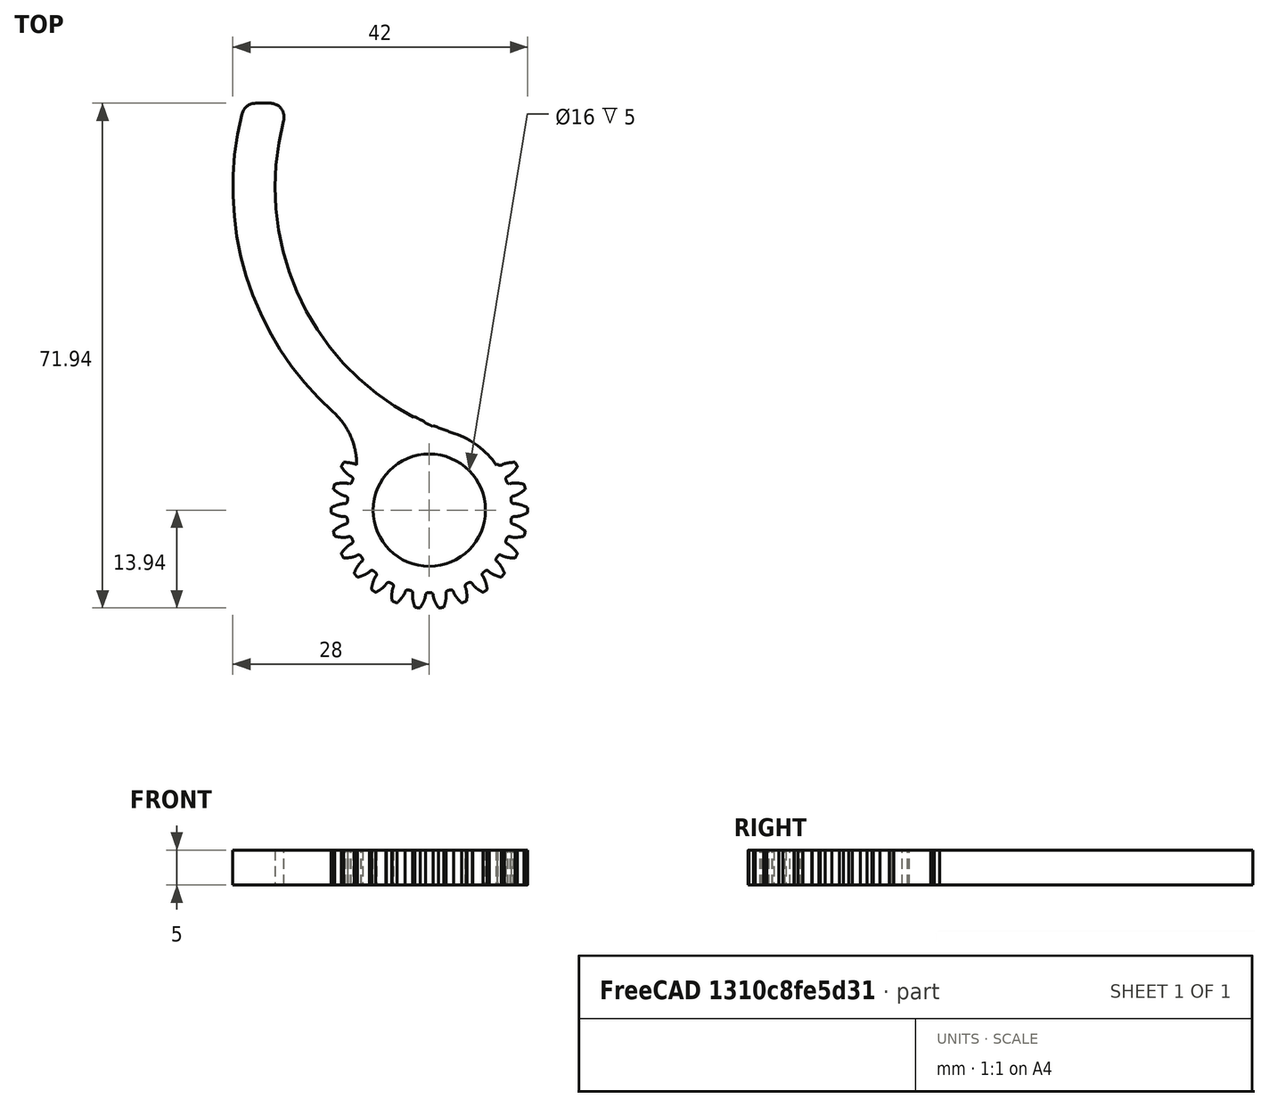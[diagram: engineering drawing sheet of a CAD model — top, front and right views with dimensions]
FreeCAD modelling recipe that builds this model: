
FCSTD DOCUMENT  (FreeCAD 1.0R39109 (Git))
Label: BrasV1_R
License: All rights reserved
LicenseURL: https://en.wikipedia.org/wiki/All_rights_reserved
objects: Sketcher::SketchObject×3, PartDesign::Pad×2, PartDesign::Fillet×2, PartDesign::Pocket×2, PartDesign::Chamfer×1, PartDesign::Line×1, Part::Part2DObjectPython×1, Mesh::Feature×1, PartDesign::CoordinateSystem×1, PartDesign::Body×1
note: 31 computed .brp shape members not serialized (recipe doc carries the construction recipe); baked Part::Feature solids carry a one-line shape summary decoded from their .brp

FEATURE [Sketcher::SketchObject] Sketch
  ArcFitTolerance = 0
  AttachmentSupport = -> [XY_Plane]
  FullyConstrained = true
  MakeInternals = false
  MapMode = 5
  sketch-geometry (5):
    g0: ArcOfCircle CenterX=0 CenterY=0 CenterZ=0 NormalX=0 NormalY=0 NormalZ=1 AngleXU=0 Radius=37 StartAngle=2.8113 EndAngle=4.39717
    g1: Circle CenterX=-15 CenterY=-46 CenterZ=0 NormalX=0 NormalY=0 NormalZ=1 AngleXU=0 Radius=8
    g2: ArcOfCircle CenterX=-15 CenterY=-46 CenterZ=0 NormalX=0 NormalY=0 NormalZ=1 AngleXU=0 Radius=11.3839 StartAngle=2.22683 EndAngle=7.53877
    g3: ArcOfCircle CenterX=0 CenterY=0 CenterZ=0 NormalX=0 NormalY=0 NormalZ=1 AngleXU=0 Radius=43 StartAngle=2.85877 EndAngle=4.17683
    g4: LineSegment StartX=-41.2916 StartY=12 StartZ=0 EndX=-35 EndY=12 EndZ=0
  constraints (14):
    c: Coincident(g0,g-1)
    c: Radius(g0) = 37
    c: Distance(g0,g-2) = 35
    c: Diameter(g1) = 16
    c: Distance(g1,g-2) = 15
    c: Coincident(g2,g1)
    c: Tangent(g2,g0) = 1.5708
    c: Coincident(g3,g0)
    c: Coincident(g2,g3)
    c: Radius(g3) = 43
    c: Coincident(g4,g3)
    c: Coincident(g4,g0)
    c: Horizontal(g4)
    c: Distance(g1,g-1) = 46
FEATURE [PartDesign::Pad] Pad
  Direction = (0,0,1)
  Length = 5
  Length2 = 10
  Midplane = true
  Profile = -> Sketch
  ReferenceAxis = -> Sketch [N_Axis]
  Suppressed = false
  Type = 0
FEATURE [PartDesign::Fillet] Fillet
  Base = -> Pad [Edge8]
  BaseFeature = -> Pad
  Radius = 10
  SupportTransform = false
  Suppressed = false
  UseAllEdges = false
FEATURE [PartDesign::Fillet] Fillet001
  Base = -> Fillet [Edge17,Edge12]
  BaseFeature = -> Fillet
  Radius = 2
  SupportTransform = false
  Suppressed = false
  UseAllEdges = false
FEATURE [PartDesign::Chamfer] Chamfer
  Angle = 45
  Base = -> Fillet001 [Edge24,Edge8]
  BaseFeature = -> Fillet001
  ChamferType = 0
  FlipDirection = false
  Size = 0.8
  Size2 = 1
  SupportTransform = false
  Suppressed = false
  UseAllEdges = false
FEATURE [PartDesign::Line] DatumLine
  AttacherType = Attacher::AttachEngineLine
  AttachmentSupport = -> [Chamfer]
  Length = 20
  MapMode = 42
  Placement = pos=(-15,-46,-1e-16) rot=(0,0,1;0rad)
  ResizeMode = 0
FEATURE [Part::Part2DObjectPython] InvoluteGear  # Draft 2D object (typed FeaturePython)
  AddendumCoefficient = 1
  DedendumCoefficient = 1.25
  ExternalGear = true
  HighPrecision = true
  Modules = 1
  NumberOfTeeth = 26
  Placement = pos=(-15,-46,0) rot=(0,0,20;0rad)
  PressureAngle = 20
  ProfileShiftCoefficient = 0
  RootFilletCoefficient = 0.38
FEATURE [PartDesign::Pad] Pad001
  BaseFeature = -> Chamfer
  Direction = (0,0,1)
  Length = 5
  Length2 = 10
  Midplane = true
  Profile = -> InvoluteGear
  ReferenceAxis = -> InvoluteGear [N_Axis]
  Suppressed = false
  Type = 0
FEATURE [Sketcher::SketchObject] Sketch001
  ArcFitTolerance = 0
  AttachmentSupport = -> [Pad001]
  FullyConstrained = false
  MakeInternals = false
  MapMode = 5
  Placement = pos=(0,0,2.5) rot=(0,0,1;0rad)
  sketch-geometry (1):
    g0: Circle CenterX=-15 CenterY=-46 CenterZ=0 NormalX=0 NormalY=0 NormalZ=1 AngleXU=0 Radius=8
  constraints (1):
    c: Diameter(g0) = 16
FEATURE [PartDesign::Pocket] Pocket
  BaseFeature = -> Pad001
  Direction = (0,0,-1)
  Length = 5
  Length2 = 5
  Profile = -> Sketch001
  ReferenceAxis = -> Sketch001 [N_Axis]
  Suppressed = false
  Type = 1
FEATURE [Sketcher::SketchObject] Sketch002
  ArcFitTolerance = 0
  AttachmentSupport = -> [Pocket]
  ExternalGeometry = -> [Pocket]
  FullyConstrained = true
  MakeInternals = false
  MapMode = 5
  Placement = pos=(0,0,2.5) rot=(0,0,1;0rad)
  sketch-geometry (4):
    g0: ArcOfCircle CenterX=-15 CenterY=-46 CenterZ=0 NormalX=0 NormalY=0 NormalZ=1 AngleXU=0 Radius=11.5 StartAngle=0.593412 EndAngle=1.25558
    g1: ArcOfCircle CenterX=-15 CenterY=-46 CenterZ=0 NormalX=0 NormalY=0 NormalZ=1 AngleXU=0 Radius=15 StartAngle=0.593412 EndAngle=1.84626
    g2: LineSegment StartX=-5.46607 StartY=-39.5693 StartZ=0 EndX=-2.56444 EndY=-37.6121 EndZ=0
    g3: ArcOfCircle CenterX=0 CenterY=0 CenterZ=0 NormalX=0 NormalY=0 NormalZ=1 AngleXU=0 Radius=36.8839 StartAngle=4.1687 EndAngle=4.39717
  constraints (11):
    c: Coincident(g0,g-3)
    c: Coincident(g1,g0)
    c: Coincident(g2,g0)
    c: Coincident(g2,g1)
    c: Coincident(g1,g3)
    c: Tangent(g3,g0) = 1.5708
    c: Perpendicular(g0,g2)
    c: Radius(g0) = 11.5
    c: Coincident(g3,g-1)
    c: Radius(g1) = 15
    c: Angle(g-1,g2) = 0.593412
FEATURE [PartDesign::Pocket] Pocket001
  BaseFeature = -> Pocket
  Direction = (0,0,-1)
  Length = 5
  Length2 = 5
  Profile = -> Sketch002
  ReferenceAxis = -> Sketch002 [N_Axis]
  Suppressed = false
  Type = 0
FEATURE [Mesh::Feature] Mesh  label="Corps (Meshed)"
FEATURE [PartDesign::CoordinateSystem] LCS_1
  AttacherType = Attacher::AttachEngine3D
  AttachmentSupport = -> [Pocket001]
  MapMode = 11
  Placement = pos=(-15,-46,2.5) rot=(0,0,1;1.5708rad)
FEATURE [PartDesign::Body] Body  label="bras_R"
  AllowCompound = false
  Group = -> [Sketch,Pad,Fillet,Fillet001,Chamfer,DatumLine,InvoluteGear,Pad001,Sketch001,Pocket,Sketch002,Pocket001,LCS_1]
  Origin = -> Origin
  Tip = -> Pocket001
